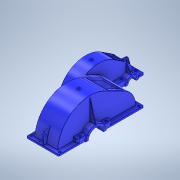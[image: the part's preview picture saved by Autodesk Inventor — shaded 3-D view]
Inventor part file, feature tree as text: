
AUTODESK INVENTOR PART (.ipt)
format: ipt  version: 2020 (Build 240168000, 168)  size: 2,550,784 bytes
history: native  units: mm
features: sketch x87, extrude x70, projected_geometry x45, plane x34, other x25, hole x17, mirror x14, fillet x14, reference x7
ambient origin geometry x8: Origin, YZ Plane, XZ Plane, XY Plane, X Axis, Y Axis, Z Axis, Center Point
bodies: 实体1 (feature_tree), 实体2 (feature_tree)
feature tree (313):
  plane  "工作平面1"
  extrude  "拉伸1"  Depth=10.0mm TaperAngle=0.0deg
  plane  "工作平面2"
  extrude  "拉伸2"  Depth=10.0mm TaperAngle=0.0deg
  plane  "工作平面3"
  extrude  "拉伸3"  Depth=10.0mm TaperAngle=0.0deg
  plane  "工作平面4"
  extrude  "拉伸4"  Depth=15.0mm TaperAngle=0.0deg
  plane  "工作平面5"
  extrude  "拉伸5"  [1 undecoded]
  sketch  "草图7"  dims[d52=10.0mm d53=0.0mm d54=10.0mm d55=0.0mm]
  plane  "工作平面6"
  extrude  "拉伸6"  Depth=10.0mm
  plane  "工作平面7"
  extrude  "拉伸7"  Depth=15.0mm
  extrude  "拉伸8"  Depth=10.0mm TaperAngle=0.0deg
  plane  "工作平面8"
  sketch  "草图11"  dims[d56=8.0mm d57=0.0mm d58=15.0mm d59=0.0mm]
  sketch  "草图12"  dims[d60=15.0mm d61=0.0mm d62=-10.0mm]
  extrude  "拉伸9"  [1 undecoded]
  extrude  "拉伸10"  Depth=10.0mm
  other  "对称面1"
  mirror  "镜像1"
  extrude  "拉伸11"  Depth=10.0mm TaperAngle=0.0deg
  sketch  "草图15"  dims[d74=15.0mm d75=0.0mm d76=10.0mm d77=0.0mm]
  other  "工作面101"
  sketch  "草图16"  dims[d78=10.0mm d79=0.0mm d80=-10.0mm]
  plane  "工作平面11"
  extrude  "拉伸12"  Depth=143.0mm TaperAngle=0.0deg
  other  "对称面2"
  extrude  "拉伸13"  Depth=10.0mm TaperAngle=0.0deg
  extrude  "拉伸14"  Depth=10.0mm TaperAngle=0.0deg
  fillet  "圆角2"  Radius=10.0mm
  extrude  "拉伸15"  Depth=10.0mm TaperAngle=0.0deg
  extrude  "拉伸16"  Depth=36.0mm
  mirror  "镜像2"
  extrude  "拉伸17"  Depth=35.0mm
  plane  "工作平面13"
  extrude  "拉伸18"  Depth=10.0mm TaperAngle=0.0deg
  plane  "工作平面14"
  extrude  "拉伸19"  Depth=10.0mm TaperAngle=0.0deg
  plane  "工作平面15"
  extrude  "拉伸20"  Depth=10.0mm TaperAngle=0.0deg
  other  "合并1"
  extrude  "拉伸21"  Depth=8.0mm TaperAngle=0.0deg
  mirror  "镜像3"
  extrude  "拉伸22"  Depth=5.0mm TaperAngle=0.0deg
  mirror  "镜像4"
  plane  "工作平面16"
  extrude  "拉伸23"  Depth=5.0mm TaperAngle=0.0deg
  extrude  "拉伸24"  Depth=36.0mm
  extrude  "拉伸25"  Depth=50.0mm
  sketch  "草图34"  dims[d131=5.0mm d132=0.0mm d133=5.0mm d134=0.0mm]
  extrude  "拉伸26"  Depth=7.0mm TaperAngle=0.0deg
  extrude  "拉伸27"  Depth=10.0mm TaperAngle=0.0deg
  sketch  "草图36"  dims[d138=5.0mm d139=0.0mm d140=50.0mm]
  extrude  "拉伸28"  Depth=70.0mm
  extrude  "拉伸29"  Depth=15.0mm TaperAngle=0.0deg
  extrude  "拉伸30"  Depth=23.0mm
  extrude  "拉伸31"  Depth=10.0mm TaperAngle=0.0deg
  extrude  "拉伸32"  Depth=36.0mm
  extrude  "拉伸33"  Depth=10.0mm TaperAngle=0.0deg
  extrude  "拉伸34"  Depth=10.0mm TaperAngle=0.0deg
  extrude  "拉伸35"  Depth=46.0mm TaperAngle=0.0deg
  extrude  "拉伸36"  Depth=12.0mm
  extrude  "拉伸37"  Depth=100.0mm
  other  "对称面4"
  mirror  "镜像5"
  extrude  "拉伸38"  Depth=46.0mm TaperAngle=0.0deg
  sketch  "草图48"  dims[d178=20.0mm d179=100.0mm]
  extrude  "拉伸39"  Depth=10.0mm TaperAngle=0.0deg
  extrude  "拉伸40"  Depth=10.0mm TaperAngle=0.0deg
  extrude  "拉伸41"  Depth=10.0mm
  extrude  "拉伸42"  [1 undecoded]
  extrude  "拉伸43"  [1 undecoded]
  extrude  "拉伸44"  Depth=10.0mm TaperAngle=0.0deg
  sketch  "草图53"  dims[d193=10.0mm d194=0.0mm d195=-10.0mm]
  extrude  "拉伸45"  Depth=113.0mm
  extrude  "拉伸46"  TaperAngle=0.0deg  [1 undecoded]
  extrude  "拉伸47"  Depth=206.0mm
  extrude  "拉伸48"  TaperAngle=0.0deg  [1 undecoded]
  extrude  "拉伸49"  Depth=1.0mm
  extrude  "拉伸50"  Depth=1.0mm
  other  "工作轴2"
  extrude  "拉伸51"  Depth=1.0mm
  plane  "工作平面19"
  mirror  "镜像6"
  plane  "工作平面20"
  mirror  "镜像7"
  fillet  "圆角3"  Radius=16.580628mm
  fillet  "圆角4"  Radius=19.198622mm
  sketch  "草图60"  dims[d213=180.0mm d214=0.0mm]
  extrude  "拉伸52"  Depth=1.0mm
  extrude  "拉伸53"  Depth=20.0mm
  extrude  "拉伸54"  TaperAngle=105.0deg  [1 undecoded]
  extrude  "拉伸55"  Depth=110.0mm
  extrude  "拉伸56"  Depth=20.0mm
  extrude  "拉伸57"  Depth=90.0mm
  plane  "工作平面21"
  plane  "工作平面22"
  extrude  "拉伸58"  Depth=90.0mm
  extrude  "拉伸59"  Depth=140.0mm
  extrude  "拉伸60"  Depth=4.0mm TaperAngle=0.0deg
  extrude  "拉伸61"  Depth=110.0mm
  extrude  "拉伸63"  [1 undecoded]
  plane  "工作平面23"
  plane  "工作平面24"
  plane  "工作平面25"
  other  "加强筋1"
  mirror  "镜像8"
  other  "加强筋2"
  other  "加强筋3"
  mirror  "镜像9"
  sketch  "草图77"  dims[d291=120.0mm d292=90.0mm]
  other  "加强筋5"
  fillet  "圆角6"  Radius=30.0mm
  hole  "孔2"  [1 undecoded]
  other  "第一对称面"
  sketch  "草图79"  dims[d293=130.0mm d294=140.0mm]
  other  "加强筋6"
  hole  "孔3"  [1 undecoded]
  fillet  "圆角7"  Radius=20.0mm
  other  "第二对称面"
  plane  "工作平面28"
  plane  "工作平面29"
  plane  "工作平面30"
  hole  "孔4"  [1 undecoded]
  sketch  "草图82"  dims[d316=18.0mm d317=110.0mm]
  extrude  "拉伸65"  Depth=170.0mm
  hole  "孔6"  [1 undecoded]
  plane  "工作平面32"
  extrude  "拉伸66"  Depth=100.0mm
  hole  "孔7"  [1 undecoded]
  plane  "工作平面34"
  extrude  "拉伸67"  Depth=6.0mm
  hole  "孔8"  [1 undecoded]
  extrude  "拉伸68"  Depth=35.0mm
  hole  "孔9"  [1 undecoded]
  mirror  "镜像10"
  hole  "孔10"  [1 undecoded]
  extrude  "拉伸69"  Depth=105.0mm
  extrude  "拉伸70"  TaperAngle=30.0deg  [1 undecoded]
  fillet  "圆角8"  Radius=28.0mm
  fillet  "圆角9"  Radius=28.0mm
  hole  "孔11"  [1 undecoded]
  hole  "孔12"  [1 undecoded]
  extrude  "拉伸71"  Depth=12.0mm
  extrude  "拉伸72"  Depth=2.0mm
  hole  "孔13"  [1 undecoded]
  plane  "工作平面35"
  mirror  "镜像11"
  plane  "工作平面36"
  hole  "孔14"  [1 undecoded]
  hole  "孔15"  [1 undecoded]
  mirror  "镜像12"
  hole  "孔16"  [1 undecoded]
  other  "工作轴3"
  other  "工作轴4"
  other  "工作轴5"
  plane  "工作平面39"
  sketch  "草图104"  dims[d410=60.0mm d412=360.0deg]
  hole  "孔17"  [1 undecoded]
  mirror  "镜像13"
  plane  "工作平面40"
  hole  "孔18"  [1 undecoded]
  mirror  "镜像14"
  plane  "工作平面41"
  hole  "孔19"  [1 undecoded]
  fillet  "圆角10"  Radius=0.15mm
  fillet  "圆角11"  Radius=0.25mm
  fillet  "圆角12"  Radius=0.375mm
  fillet  "圆角13"  Radius=14.3117mm
  fillet  "圆角14"  [1 undecoded]
  fillet  "圆角15"  [1 undecoded]
  fillet  "圆角16"  [1 undecoded]
  sketch  "草图2"  dims[d0=41.0mm d1=40.0mm d2=41.0mm d3=8.0mm d4=41.0mm d5=41.0mm d6=40.0mm d7=8.0mm d8=25.0mm d9=71.0mm d10=8.0mm d11=70.0mm d12=190.0mm d13=75.0mm d14=43.0mm d15=8.0mm d16=75.0mm d17=40.0mm d18=31.0mm d19=12.0mm d20=25.0mm d21=10.0mm d22=8.0mm d23=30.0mm d24=5.0mm d25=25.0mm d26=174.0mm d27=91.0mm d28=40.0mm d29=21.0mm d30=71.0mm d31=12.0mm d32=30.0mm d33=30.0mm d34=25.0mm d35=12.0mm d36=30.0mm d37=30.0mm d38=100.0mm d39=40.0mm d40=12.0mm d41=20.0mm d42=70.0mm d43=15.0mm d44=2.0mm d45=31.0mm d46=10.0mm d47=0.0mm]
  sketch  "草图6"  dims[d48=10.0mm d49=0.0mm d50=10.0mm d51=0.0mm]
  projected_geometry  "投影回路1"
  sketch  "草图13"  dims[d66=130.0mm d71=10.0mm]
  projected_geometry  "投影回路2"
  sketch  "草图14"  dims[d72=150.0mm d73=15.0mm]
  sketch  "草图17"  dims[d82=10.0mm d83=10.0mm]
  projected_geometry  "投影回路3"
  projected_geometry  "投影回路4"
  sketch  "草图18"  dims[d84=-10.0mm d85=10.0mm d86=0.0mm]
  projected_geometry  "投影回路5"
  sketch  "草图19"  dims[d87=10.0mm d88=0.0mm d90=143.0mm d91=0.0mm]
  projected_geometry  "投影回路6"
  sketch  "草图22"  dims[d92=6.0mm d93=10.0mm d94=0.0mm]
  sketch  "草图24"  dims[d95=10.0mm d96=0.0mm d97=10.0mm d98=0.0mm d99=10.0mm d100=0.0mm]
  sketch  "草图25"  dims[d101=10.0mm d102=0.0mm d103=10.0mm d104=0.0mm]
  sketch  "草图26"  dims[d105=10.0mm d106=0.0mm d107=36.0mm]
  projected_geometry  "投影回路7"
  projected_geometry  "投影回路8"
  sketch  "草图27"  dims[d108=10.0mm d109=0.0mm d110=35.0mm]
  sketch  "草图28"  dims[d111=10.0mm d112=0.0mm d113=10.0mm d114=0.0mm]
  projected_geometry  "投影回路9"
  sketch  "草图29"  dims[d115=10.0mm d116=0.0mm d117=10.0mm d118=0.0mm]
  sketch  "草图31"  dims[d119=10.0mm d120=0.0mm d121=10.0mm d122=0.0mm]
  projected_geometry  "投影回路11"
  sketch  "草图32"  dims[d123=8.0mm d124=0.0mm d125=8.0mm d126=0.0mm]
  projected_geometry  "投影回路12"
  sketch  "草图33"  dims[d127=5.0mm d128=0.0mm d129=5.0mm d130=0.0mm]
  projected_geometry  "投影回路13"
  projected_geometry  "投影回路14"
  sketch  "草图35"  dims[d135=5.0mm d136=0.0mm d137=36.0mm]
  projected_geometry  "投影回路15"
  sketch  "草图37"  dims[d141=5.0mm d142=0.0mm d143=7.0mm d144=0.0mm]
  projected_geometry  "投影回路16"
  sketch  "草图38"  dims[d145=10.0mm d146=0.0mm d147=10.0mm d148=0.0mm]
  projected_geometry  "投影回路17"
  sketch  "草图39"  dims[d149=10.0mm d150=0.0mm d151=70.0mm]
  projected_geometry  "投影回路18"
  sketch  "草图40"  dims[d152=10.0mm d153=0.0mm d154=15.0mm d155=0.0mm]
  projected_geometry  "投影回路19"
  sketch  "草图41"  dims[d156=23.0mm d157=0.0mm d158=23.0mm]
  projected_geometry  "投影回路20"
  projected_geometry  "投影回路21"
  sketch  "草图42"  dims[d159=36.0mm d160=10.0mm d161=0.0mm]
  projected_geometry  "投影回路22"
  sketch  "草图43"  dims[d162=23.0mm d163=36.0mm]
  projected_geometry  "投影回路23"
  sketch  "草图44"  dims[d164=10.0mm d165=0.0mm d166=10.0mm d167=0.0mm]
  sketch  "草图45"  dims[d168=10.0mm d169=0.0mm d170=10.0mm d171=0.0mm]
  sketch  "草图46"  dims[d172=70.0mm d173=46.0mm d174=0.0mm]
  sketch  "草图47"  dims[d175=10.0mm d176=0.0mm d177=12.0mm]
  projected_geometry  "投影回路24"
  sketch  "草图49"  dims[d180=46.0mm d181=0.0mm d182=46.0mm d183=0.0mm]
  projected_geometry  "投影回路25"
  sketch  "草图50"  dims[d184=380.0mm d185=10.0mm d186=0.0mm]
  sketch  "草图51"  dims[d187=390.0mm d188=10.0mm d189=0.0mm]
  projected_geometry  "投影回路26"
  sketch  "草图52"  dims[d190=10.0mm d191=0.0mm d192=10.0mm]
  projected_geometry  "投影回路27"
  sketch  "草图54"  dims[d196=10.0mm d197=-10.0mm]
  projected_geometry  "投影回路28"
  sketch  "草图55"  dims[d198=10.0mm d199=0.0mm d200=10.0mm d201=0.0mm]
  projected_geometry  "投影回路29"
  sketch  "草图56"  dims[d202=10.0mm d203=0.0mm d204=113.0mm]
  projected_geometry  "投影回路30"
  sketch  "草图57"  dims[d205=120.0mm d206=0.0mm]
  sketch  "草图58"  dims[d207=2.0mm d208=0.0mm d212=206.0mm]
  projected_geometry  "投影回路31"
  projected_geometry  "投影回路42"
  projected_geometry  "投影回路43"
  sketch  "草图61"  dims[d215=2.0mm d216=0.0mm d220=1.0mm]
  sketch  "草图62"  dims[d221=9.0mm d222=0.0mm d223=0.0mm d224=1.0mm d225=1.0mm d226=1.0mm]
  sketch  "草图63"  dims[d227=9.0mm d228=0.0mm d229=0.0mm d230=1.0mm d231=1.0mm d232=1.0mm]
  sketch  "草图64"  dims[d233=9.0mm d234=0.0mm d235=0.0mm d236=1.0mm d237=1.0mm d255=16.580628mm d256=19.198622mm]
  projected_geometry  "投影回路44"
  projected_geometry  "投影回路45"
  projected_geometry  "投影回路46"
  projected_geometry  "投影回路47"
  sketch  "草图65"  dims[d257=115.0mm d258=1.0mm]
  sketch  "草图66"  dims[d259=12.0mm d260=0.0mm d261=0.0mm d262=1.0mm d263=1.0mm d264=20.0mm]
  sketch  "草图67"  dims[d265=20.0mm d266=6.0mm d267=45.0mm d268=2.0mm d269=90.0deg d270=8.0mm d271=20.594885mm d272=105.0deg]
  projected_geometry  "投影回路48"
  sketch  "草图68"  dims[d273=19.198622mm d274=110.0mm]
  sketch  "草图70"  dims[d275=1.0mm]
  sketch  "草图72"  dims[d276=12.0mm d277=0.0mm d278=0.0mm d279=1.0mm d280=1.0mm]
  sketch  "草图73"  dims[d281=20.0mm d282=6.0mm d283=26.0mm d284=2.0mm d285=90.0deg d286=8.0mm d287=20.594885mm d288=20.0mm]
  sketch  "草图74"  dims[d289=70.0mm d290=90.0mm]
  projected_geometry  "投影回路52"
  projected_geometry  "投影回路53"
  projected_geometry  "投影回路54"
  sketch  "草图81"  dims[d295=13.5mm d296=6.0mm d297=26.0mm d298=2.0mm d299=90.0deg d300=8.0mm d301=20.594885mm d302=4.0mm d303=0.0mm]
  sketch  "草图83"  dims[d318=10.0mm d319=6.0mm d320=26.0mm d321=2.0mm d322=90.0deg d323=8.0mm d324=20.594885mm d325=-3.0mm d326=30.0mm]
  sketch  "草图85"  dims[d327=10.0mm d328=0.0mm]
  plane  "工作平面31"
  sketch  "草图86"  dims[d329=15.29367mm d330=36.0mm d331=18.0mm d332=2.0mm d333=90.0deg d334=47.2mm d335=0.0mm d336=-3.0mm]
  sketch  "草图87"  dims[d337=30.0mm d338=10.0mm d339=0.0mm]
  plane  "工作平面33"
  sketch  "草图88"  dims[d340=15.29367mm d341=36.0mm d342=18.0mm d343=2.0mm d344=90.0deg d345=47.2mm d346=0.0mm d347=20.0mm d348=0.0mm]
  sketch  "草图89"  dims[d349=36.001mm d350=70.0mm]
  sketch  "草图90"  dims[d351=13.5mm d352=36.0mm d353=26.0mm d354=2.0mm d355=90.0deg d356=8.0mm d357=0.0mm]
  projected_geometry  "投影回路56"
  sketch  "草图91"  dims[d358=13.5mm d359=6.0mm d360=26.0mm d361=2.0mm d362=90.0deg d363=8.0mm d364=0.0mm d365=170.0mm]
  sketch  "草图92"  dims[d366=150.0mm d367=15.0mm]
  reference  "参考1"
  reference  "参考2"
  reference  "参考3"
  reference  "参考4"
  reference  "参考5"
  sketch  "草图93"  dims[d368=4.0mm d369=0.0mm d370=100.0mm]
  sketch  "草图94"  dims[d371=80.0mm d372=10.0mm]
  sketch  "草图95"  dims[d373=10.0mm d374=0.0mm d375=6.0mm]
  sketch  "草图96"  dims[d376=6.0mm]
  sketch  "草图97"  dims[d377=4.917mm d378=12.0mm d379=26.0mm d380=2.0mm d381=90.0deg d382=17.1mm d383=0.0mm]
  sketch  "草图98"  dims[d384=4.917mm d385=12.0mm d386=26.0mm d387=2.0mm d388=90.0deg d389=17.1mm d390=0.0mm d391=35.0mm]
  sketch  "草图100"  dims[d392=2.0mm d393=0.0mm d394=35.0mm]
  sketch  "草图101"  dims[d395=2.0mm d396=0.0mm d397=175.0mm]
  sketch  "草图102"  dims[d398=60.0mm d400=360.0deg]
  sketch  "草图103"  dims[d402=8.376mm d403=15.0mm d404=4.0mm d405=2.0mm d406=90.0deg d407=18.0mm d408=20.594885mm d409=165.0mm]
  reference  "参考8"
  projected_geometry  "投影回路57"
  plane  "工作平面37"
  plane  "工作平面38"
  reference  "参考9"
  projected_geometry  "投影回路58"
  sketch  "草图105"  dims[d414=8.376mm d415=15.0mm d416=4.0mm d417=2.0mm d418=90.0deg d419=18.0mm d420=20.594885mm d421=105.0mm]
  sketch  "草图106"  dims[d422=60.0mm d424=360.0deg]
  projected_geometry  "投影回路59"
  sketch  "草图107"  dims[d426=8.376mm d427=15.0mm d428=4.0mm d429=2.0mm d430=90.0deg d431=18.0mm d432=20.594885mm d433=8.376mm d434=15.0mm d435=4.0mm d436=2.0mm d437=90.0deg d438=18.0mm d439=20.594885mm d440=30.0deg d441=28.0mm d442=6.647mm d443=16.0mm d444=4.0mm d445=2.0mm d446=90.0deg d447=22.2mm d448=20.594885mm d449=28.0mm d450=6.647mm d451=16.0mm d452=4.0mm d453=2.0mm d454=90.0deg d455=22.2mm d456=20.594885mm d457=28.0mm d458=6.647mm d459=16.0mm d460=4.0mm d461=2.0mm d462=90.0deg d463=22.2mm d464=20.594885mm d465=20.0mm d466=12.0mm d467=2.0mm d468=1.0mm d469=2.0mm d470=2.0mm d471=2.0mm d248=1.0mm d249=1.0mm d250=1.0mm d251=0.15mm d252=0.25mm d253=0.375mm d254=14.3117mm]
  projected_geometry  "投影回路60"
  other  "<userpath>\Desktop\ME_course_project\课设试试\shaft_try_1.iam"
  other  "shaft_try_1.iam"
  other  "低速级"
  other  "正齿轮2:1"
  other  "xia(1):1"
  other  "<userpath>\Desktop\111111\Workspace\cpz assemble.iam"
  other  "cpz assemble.iam"
  other  "轴承通盖:1"
  other  "轴承通盖1:1"
note: 29 required parameter values undecoded (feature->parameter linkage not recoverable at this tier; creation-order binding heuristic only, values carry confidence <= 0.55)
